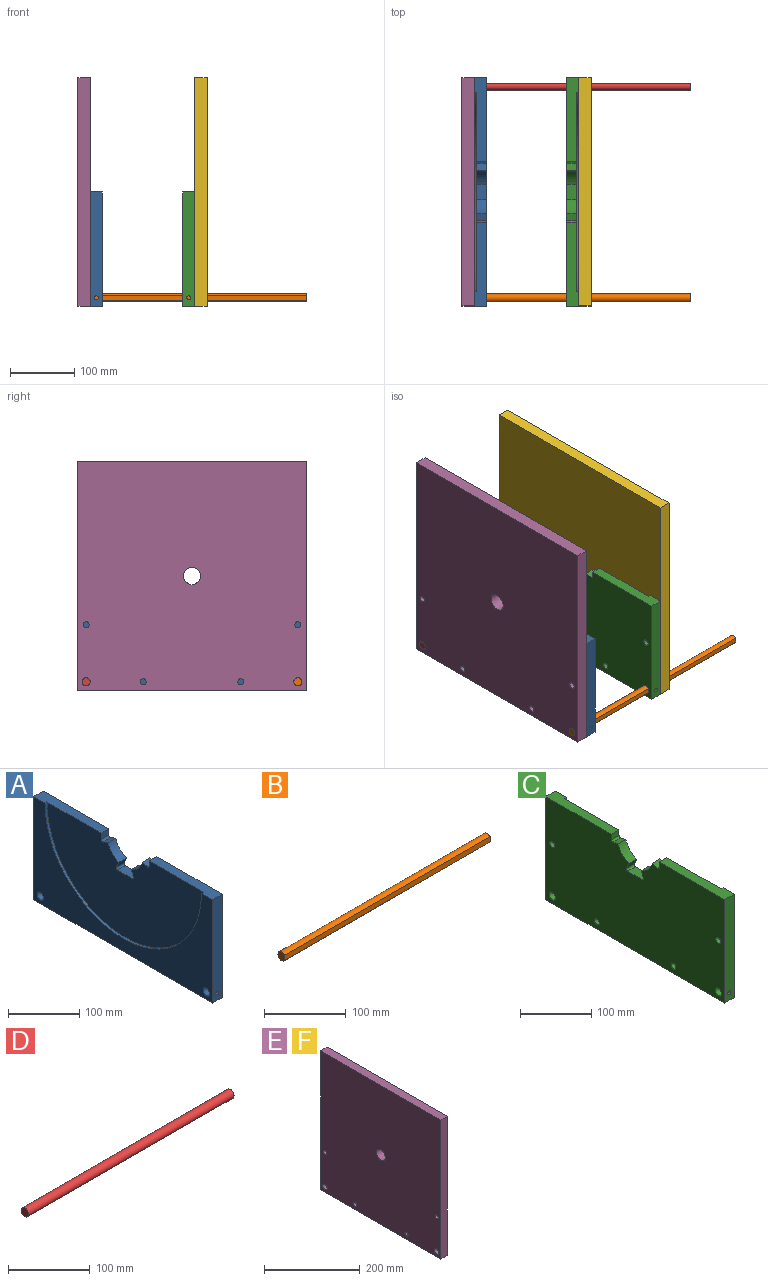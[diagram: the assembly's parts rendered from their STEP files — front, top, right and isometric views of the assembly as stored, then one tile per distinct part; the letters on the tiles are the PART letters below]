
ASSEMBLY  parts=6 mates=6
PART A: 26 faces, bbox 19.1x355.6x177.8 mm
  f0: plane 355.6x177.8mm, normal (1,0,0), area 60354.6mm2, adj f2,f3,f4,f5,f6,f7,f8,f9
  f1: plane 311.15x155.58mm, normal (-1,0,0), area 35401.2mm2, adj f2,f3,f4,f5,f6,f7,f8,f9
  f2: cylinder r=34.9mm len=23.34mm, axis (-1,0,0), area 503.1mm2, adj f0,f1,f4,f25
  f3: plane 130.2x19.05mm, normal (0,0,1), area 2068.9mm2, adj f0,f1,f10,f11,f17,f23
  f4: plane 15.24x10.85mm, normal (0,0.92,-0.4), area 180.4mm2, adj f0,f1,f2,f5
  f5: cylinder r=2.54mm len=15.24mm, axis (-1,0,0), area 76.8mm2, adj f0,f1,f4,f6
  f6: plane 29.41x15.24mm, normal (0,0,1), area 448.1mm2, adj f0,f1,f5,f7
  f7: cylinder r=2.54mm len=15.24mm, axis (-1,0,0), area 76.8mm2, adj f0,f1,f6,f8
  f8: plane 15.24x11.03mm, normal (0,-0.92,-0.4), area 183.4mm2, adj f0,f1,f7,f9
  f9: cylinder r=34.9mm len=23.16mm, axis (-1,0,0), area 495.3mm2, adj f0,f1,f8,f21
  f10: plane 355.6x177.8mm, normal (-1,0,0), area 24953.4mm2, adj f3,f11,f12,f13,f14,f15,f16,f17
  f11: plane 177.8x19.05mm, normal (0,-1,0), area 3355.4mm2, adj f0,f3,f10,f16,f18
  f12: plane 130.2x19.05mm, normal (0,0,1), area 2068.9mm2, adj f0,f1,f10,f13,f17,f20
  f13: plane 177.8x19.05mm, normal (0,1,0), area 3355.4mm2, adj f0,f10,f12,f16,f19
  f14: cylinder r=6.35mm len=19.05mm, axis (-1,0,0), area 727.4mm2, adj f0,f10,f18
  f15: cylinder r=6.35mm len=19.05mm, axis (-1,0,0), area 727.5mm2, adj f0,f10,f19
  f16: plane 355.6x19.05mm, normal (0,0,-1), area 6774.2mm2, adj f0,f10,f11,f13
  f17: cylinder r=155.57mm len=311.15mm, axis (-1,0,0), area 1862.1mm2, adj f1,f3,f10,f12
  f18: cylinder r=3.17mm len=7.2mm, axis (0,-1,0), area 135mm2, adj f11,f14
  f19: cylinder r=3.17mm len=7.2mm, axis (0,1,0), area 135mm2, adj f13,f15
  f20: plane 15.24x10.85mm, normal (0,-1,0), area 165.4mm2, adj f0,f1,f12,f22
  f21: plane 15.24x10.6mm, normal (0,0.34,0.94), area 171.7mm2, adj f0,f1,f9,f22
  f22: cylinder r=2.54mm len=15.24mm, axis (1,0,0), area 74.1mm2, adj f0,f1,f20,f21
  f23: plane 15.24x9.5mm, normal (0,1,0), area 144.8mm2, adj f0,f1,f3,f24
  f24: cylinder r=2.54mm len=15.24mm, axis (1,0,0), area 69.7mm2, adj f0,f1,f23,f25
  f25: plane 15.24x10.88mm, normal (0,-0.23,0.97), area 170.3mm2, adj f0,f1,f2,f24
PART B: 4 faces, bbox 355.6x11.4x12.7 mm
  f0: cylinder r=6.35mm len=355.6mm, axis (1,0,0), area 11281.7mm2, adj f1,f2,f3
  f1: plane 355.6x7.62mm, normal (0,-1,0), area 2709.7mm2, adj f0,f2,f3
  f2: plane 12.7x11.43mm, normal (-1,0,0), area 120.1mm2, adj f0,f1
  f3: plane 12.7x11.43mm, normal (1,0,0), area 120.1mm2, adj f0,f1
PART C: 30 faces, bbox 19.1x355.6x177.8 mm
  f0: cylinder r=34.9mm len=23.34mm, axis (1,0,0), area 503.1mm2, adj f2,f3,f4,f22
  f1: plane 130.2x19.05mm, normal (0,0,1), area 2068.9mm2, adj f2,f3,f10,f11,f17,f20
  f2: plane 355.6x177.8mm, normal (-1,0,0), area 60081.3mm2, adj f0,f1,f4,f5,f6,f7,f8,f9
  f3: plane 311.15x155.58mm, normal (1,0,0), area 35412.9mm2, adj f0,f1,f4,f5,f6,f7,f8,f9
  f4: plane 15.24x10.85mm, normal (0,0.92,-0.4), area 180.4mm2, adj f0,f2,f3,f5
  f5: cylinder r=2.54mm len=15.24mm, axis (1,0,0), area 76.8mm2, adj f2,f3,f4,f6
  f6: plane 29.41x15.24mm, normal (0,0,1), area 448.1mm2, adj f2,f3,f5,f7
  f7: cylinder r=2.54mm len=15.24mm, axis (1,0,0), area 76.8mm2, adj f2,f3,f6,f8
  f8: plane 15.24x11.03mm, normal (0,-0.92,-0.4), area 183.4mm2, adj f2,f3,f7,f9
  f9: cylinder r=34.9mm len=23.16mm, axis (1,0,0), area 495.3mm2, adj f2,f3,f8,f24
  f10: plane 355.6x177.8mm, normal (1,0,0), area 24668.4mm2, adj f1,f11,f12,f13,f14,f15,f16,f17
  f11: plane 177.8x19.05mm, normal (0,-1,0), area 3355.4mm2, adj f1,f2,f10,f16,f18
  f12: plane 130.2x19.05mm, normal (0,0,1), area 2068.9mm2, adj f2,f3,f10,f13,f17,f23
  f13: plane 177.8x19.05mm, normal (0,1,0), area 3355.4mm2, adj f2,f10,f12,f16,f19
  f14: cylinder r=6.35mm len=19.05mm, axis (1,0,0), area 727.2mm2, adj f2,f10,f18
  f15: cylinder r=6.35mm len=19.05mm, axis (1,0,0), area 727.3mm2, adj f2,f10,f19
  f16: plane 355.6x19.05mm, normal (0,0,-1), area 6774.2mm2, adj f2,f10,f11,f13
  f17: cylinder r=155.57mm len=311.15mm, axis (1,0,0), area 1862.1mm2, adj f1,f3,f10,f12
  f18: cylinder r=3.17mm len=7.2mm, axis (0,-1,0), area 135mm2, adj f11,f14
  f19: cylinder r=3.17mm len=7.2mm, axis (0,1,0), area 135mm2, adj f13,f15
  f20: plane 15.24x9.5mm, normal (0,1,0), area 144.8mm2, adj f1,f2,f3,f21
  f21: cylinder r=2.54mm len=15.24mm, axis (1,0,0), area 69.7mm2, adj f2,f3,f20,f22
  f22: plane 15.24x10.88mm, normal (0,-0.23,0.97), area 170.3mm2, adj f0,f2,f3,f21
  f23: plane 15.24x9.5mm, normal (0,-1,0), area 144.8mm2, adj f2,f3,f12,f25
  f24: plane 15.24x10.88mm, normal (0,0.23,0.97), area 170.3mm2, adj f2,f3,f9,f25
  f25: cylinder r=2.54mm len=15.24mm, axis (1,0,0), area 69.7mm2, adj f2,f3,f23,f24
  f26: cylinder r=4.76mm len=19.05mm, axis (1,0,0), area 570mm2, adj f2,f10
  f27: cylinder r=4.76mm len=19.05mm, axis (1,0,0), area 570mm2, adj f2,f10
  f28: cylinder r=4.76mm len=19.05mm, axis (1,0,0), area 570mm2, adj f2,f10
  f29: cylinder r=4.76mm len=19.05mm, axis (1,0,0), area 570mm2, adj f2,f10
PART D: 4 faces, bbox 355.6x11.4x12.7 mm
  f0: plane 355.6x7.6mm, normal (0,1,0), area 2702.9mm2, adj f1,f2,f3
  f1: cylinder r=6.34mm len=355.6mm, axis (1,0,0), area 11277mm2, adj f0,f2,f3
  f2: plane 12.69x11.42mm, normal (-1,0,0), area 119.9mm2, adj f0,f1
  f3: plane 12.69x11.42mm, normal (1,0,0), area 119.9mm2, adj f0,f1
PART E: 21 faces, bbox 19.1x355.6x355.6 mm
  f0: cylinder r=4.76mm len=12.7mm, axis (1,0,0), area 380mm2, adj f12,f20
  f1: cylinder r=4.76mm len=12.7mm, axis (1,0,0), area 380mm2, adj f12,f18
  f2: cylinder r=4.76mm len=12.7mm, axis (1,0,0), area 380mm2, adj f12,f16
  f3: cylinder r=4.76mm len=12.7mm, axis (1,0,0), area 380mm2, adj f12,f14
  f4: plane 355.6x19.05mm, normal (0,0,-1), area 6774.2mm2, adj f5,f10,f11,f12
  f5: plane 355.6x19.05mm, normal (0,1,0), area 6774.2mm2, adj f4,f6,f11,f12
  f6: plane 355.6x19.05mm, normal (0,0,1), area 6774.2mm2, adj f5,f10,f11,f12
  f7: cylinder r=13.33mm len=26.67mm, axis (-1,0,0), area 1596.1mm2, adj f11,f12
  f8: cylinder r=6.35mm len=19.05mm, axis (-1,0,0), area 760.1mm2, adj f11,f12
  f9: cylinder r=6.35mm len=19.05mm, axis (-1,0,0), area 760.1mm2, adj f11,f12
  f10: plane 355.6x19.05mm, normal (0,-1,0), area 6774.2mm2, adj f4,f6,f11,f12
  f11: plane 355.6x355.6mm, normal (1,0,0), area 125132.7mm2, adj f4,f5,f6,f7,f8,f9,f10,f13
  f12: plane 355.6x355.6mm, normal (-1,0,0), area 125354.3mm2, adj f0,f1,f2,f3,f4,f5,f6,f7
  f13: cylinder r=6.35mm len=12.7mm, axis (1,0,0), area 253.4mm2, adj f11,f14
  f14: plane 12.7x12.7mm, normal (1,0,0), area 55.4mm2, adj f3,f13
  f15: cylinder r=6.35mm len=12.7mm, axis (1,0,0), area 253.4mm2, adj f11,f16
  f16: plane 12.7x12.7mm, normal (1,0,0), area 55.4mm2, adj f2,f15
  f17: cylinder r=6.35mm len=12.7mm, axis (1,0,0), area 253.4mm2, adj f11,f18
  f18: plane 12.7x12.7mm, normal (1,0,0), area 55.4mm2, adj f1,f17
  f19: cylinder r=6.35mm len=12.7mm, axis (1,0,0), area 253.4mm2, adj f11,f20
  f20: plane 12.7x12.7mm, normal (1,0,0), area 55.4mm2, adj f0,f19
PART F: same geometry as E
PLACE A t=(811.99,71.87,-384.62)mm
PLACE B t=(1129.49,71.87,-384.62)mm
PLACE C t=(975.19,71.87,-384.62)mm
PLACE D t=(1129.49,71.87,-384.62)mm
PLACE E t=(792.94,71.87,-384.62)mm
PLACE F t=(975.19,71.87,-384.62)mm
MATE slider B.f0 <-> F.f8  axis (1,0,0) through (1148.54,-93.23,-549.72)mm
MATE fastened C.f14 <-> F.f8  axis (1,0,0) through (975.19,-93.23,-549.72)mm
MATE fastened B.f0 <-> E.f8  axis (-1,0,0) through (792.94,-93.23,-549.72)mm
MATE fastened D.f1 <-> E.f9  axis (-1,0,0) through (792.94,236.97,-549.72)mm
MATE fastened E.f8 <-> A.f14  axis (1,0,0) through (811.99,-93.23,-549.72)mm
MATE slider D.f1 <-> F.f9  axis (1,0,0) through (1148.54,236.97,-549.72)mm
